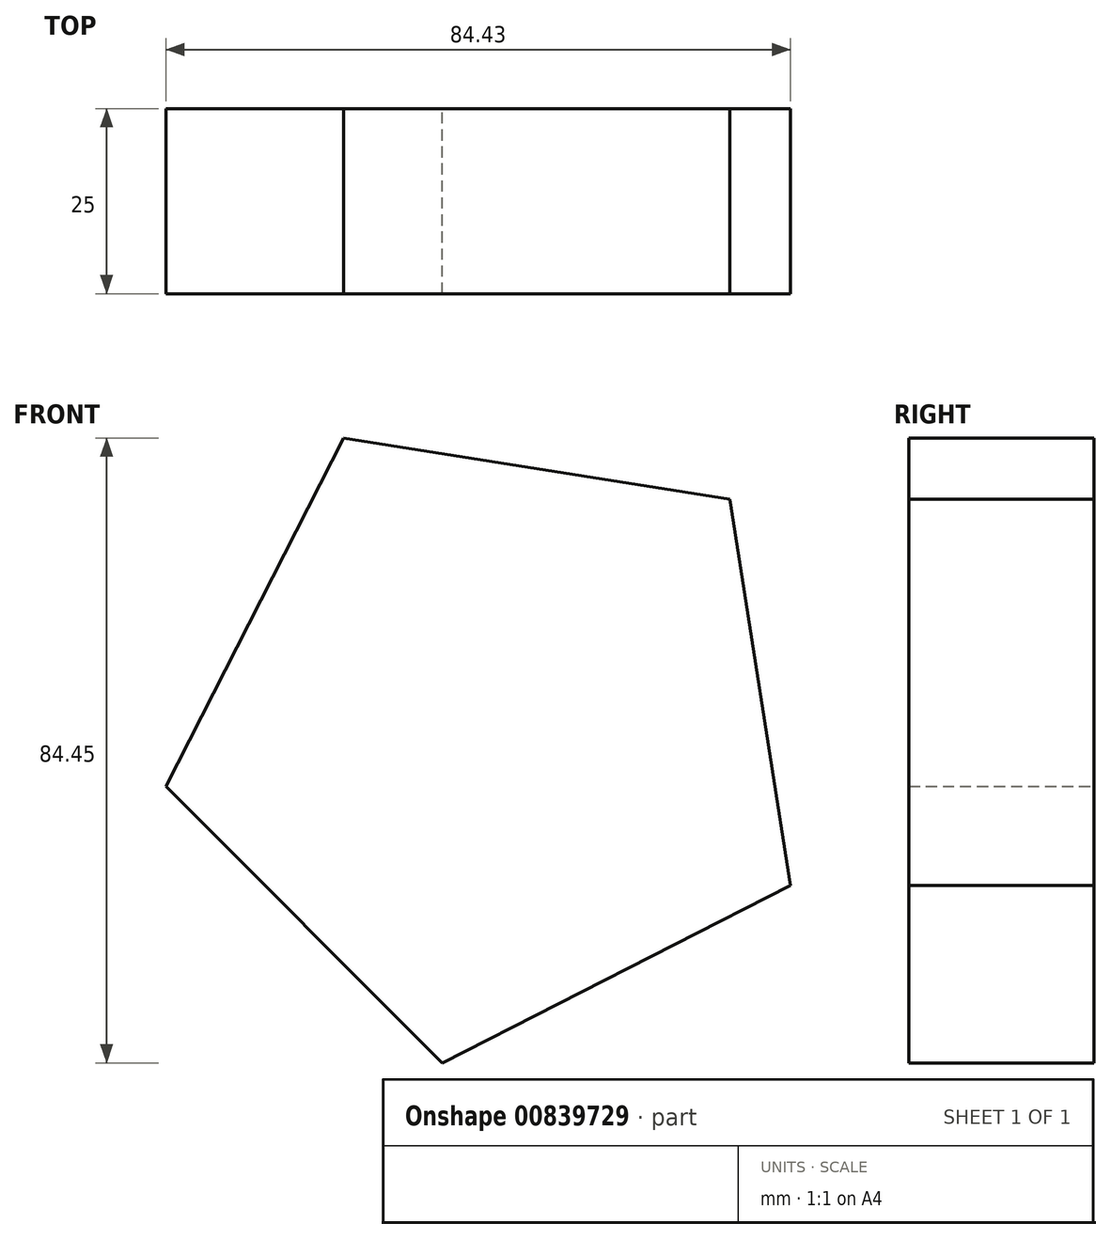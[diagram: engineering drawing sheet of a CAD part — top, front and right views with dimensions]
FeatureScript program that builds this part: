
annotation { "Feature Type Name" : "Feature", "Feature Type Description" : "" }
export const myFeature = defineFeature(function(context is Context, id is Id, definition is map)
    precondition{}
    {
        {
            var Q0;
            Q0=qCreatedBy(makeId("Front.planeOp"),FACE);
            var sketch = newSketch(context, id + "F0", { "sketchPlane" : qUnion([Q0])});
            skCircle(sketch, "E0.cCircle", {"center": v(-112.62, -10.15) * mm, "radius": 36.36 * mm, "construction": true});
            skLineSegment(sketch, "E0.0", {"start": v(-133, 29.91) * mm, "end": v(-80.82, 21.61) * mm});
            skLineSegment(sketch, "E0.1", {"start": v(-80.82, 21.61) * mm, "end": v(-72.59, -30.58) * mm});
            skLineSegment(sketch, "E0.2", {"start": v(-72.59, -30.58) * mm, "end": v(-119.68, -54.54) * mm});
            skLineSegment(sketch, "E0.3", {"start": v(-119.68, -54.54) * mm, "end": v(-157.02, -17.15) * mm});
            skLineSegment(sketch, "E0.4", {"start": v(-157.02, -17.15) * mm, "end": v(-133, 29.91) * mm});
            skPoint(sketch, "E0.0.midPoint", {"position": v(-106.91, 25.76) * mm});
            skSolve(sketch);
        }
        {
            var Q0;
            Q0 = qSketchRegion(id + "F0", true);
            extrude(context, id + "F1", {"entities" : qUnion([Q0]), "depth" : 25 * mm, "offsetDistance" : 25 * mm});
        }
    });
